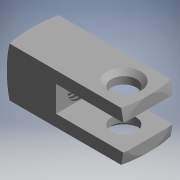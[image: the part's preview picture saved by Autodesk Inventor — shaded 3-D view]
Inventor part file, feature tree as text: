
AUTODESK INVENTOR PART (.ipt)
format: ipt  version: 2017.3 (Build 213256000, 256)  size: 193,024 bytes
history: native  units: mm (DEFAULTED — no unit token found)
features: other x126, sketch x7, revolve x4, extrude x2, thread x1, hole x1
ambient origin geometry x8: Origin, YZ Plane, XZ Plane, XY Plane, X Axis, Y Axis, Z Axis, Center Point
bodies: Solid1 (feature_tree)
feature tree (141):
  extrude  "Extrusion1"  Depth=12.7mm TaperAngle=0.0deg
  extrude  "Extrusion2"  Depth=10.6032mm TaperAngle=0.0deg
  revolve  "Revolution1"  Angle=360.0deg
  thread  "Thread1"  [1 undecoded]
  hole  "Hole1"  [1 undecoded]
  revolve  "Revolution2"  [1 undecoded]
  revolve  "Revolution3"  [1 undecoded]
  revolve  "Revolution4"  [1 undecoded]
  other  "dummy_XY"
  other  "dummy_YZ"
  other  "dummy_ZX"
  other  "dummy_X"
  other  "dummy_Y"
  other  "dummy_Z"
  other  "dummy_Center"
  other  "h1_XY"
  other  "h1_YZ"
  other  "h1_ZX"
  other  "h1_X"
  other  "h1_Y"
  other  "h1_Z"
  other  "h1_Center"
  other  "h2_XY"
  other  "h2_YZ"
  other  "h2_ZX"
  other  "h2_X"
  other  "h2_Y"
  other  "h2_Z"
  other  "h2_Center"
  other  "l1_XY"
  other  "l1_YZ"
  other  "l1_ZX"
  other  "l1_X"
  other  "l1_Y"
  other  "l1_Z"
  other  "l1_Center"
  other  "l11_XY"
  other  "l11_YZ"
  other  "l11_ZX"
  other  "l11_X"
  other  "l11_Y"
  other  "l11_Z"
  other  "l11_Center"
  other  "l12_XY"
  other  "l12_YZ"
  other  "l12_ZX"
  other  "l12_X"
  other  "l12_Y"
  other  "l12_Z"
  other  "l12_Center"
  other  "l2_XY"
  other  "l2_YZ"
  other  "l2_ZX"
  other  "l2_X"
  other  "l2_Y"
  other  "l2_Z"
  other  "l2_Center"
  other  "l21_XY"
  other  "l21_YZ"
  other  "l21_ZX"
  other  "l21_X"
  other  "l21_Y"
  other  "l21_Z"
  other  "l21_Center"
  other  "l22_XY"
  other  "l22_YZ"
  other  "l22_ZX"
  other  "l22_X"
  other  "l22_Y"
  other  "l22_Z"
  other  "l22_Center"
  other  "piston_rod_clevis_XY"
  other  "piston_rod_clevis_YZ"
  other  "piston_rod_clevis_ZX"
  other  "piston_rod_clevis_X"
  other  "piston_rod_clevis_Y"
  other  "piston_rod_clevis_Z"
  other  "piston_rod_clevis_Center"
  other  "rod_clevis_body_XY"
  other  "rod_clevis_body_YZ"
  other  "rod_clevis_body_ZX"
  other  "rod_clevis_body_X"
  other  "rod_clevis_body_Y"
  other  "rod_clevis_body_Z"
  other  "rod_clevis_body_Center"
  other  "th1_XY"
  other  "th1_YZ"
  other  "th1_ZX"
  other  "th1_X"
  other  "th1_Y"
  other  "th1_Z"
  other  "th1_Center"
  other  "th2_XY"
  other  "th2_YZ"
  other  "th2_ZX"
  other  "th2_X"
  other  "th2_Y"
  other  "th2_Z"
  other  "th2_Center"
  other  "to_cylinder_XY"
  other  "to_cylinder_YZ"
  other  "to_cylinder_ZX"
  other  "to_cylinder_X"
  other  "to_cylinder_Y"
  other  "to_cylinder_Z"
  other  "to_cylinder_Center"
  other  "w1_XY"
  other  "w1_YZ"
  other  "w1_ZX"
  other  "w1_X"
  other  "w1_Y"
  other  "w1_Z"
  other  "w1_Center"
  other  "w11_XY"
  other  "w11_YZ"
  other  "w11_ZX"
  other  "w11_X"
  other  "w11_Y"
  other  "w11_Z"
  other  "w11_Center"
  other  "w12_XY"
  other  "w12_YZ"
  other  "w12_ZX"
  other  "w12_X"
  other  "w12_Y"
  other  "w12_Z"
  other  "w12_Center"
  other  "w2_XY"
  other  "w2_YZ"
  other  "w2_ZX"
  other  "w2_X"
  other  "w2_Y"
  other  "w2_Z"
  other  "w2_Center"
  sketch  "Sketch_1"  dims[d0=12.7mm d1=0.0mm d2=12.7mm d3=0.0mm]
  sketch  "Sketch_2"  dims[d4=360.0deg d5=10.6032mm d6=0.0mm]
  sketch  "Sketch_3"  dims[d7=6.79196mm d8=6.0mm d9=4.0mm d10=2.0mm d11=90.0deg d12=1.524mm d13=0.0mm d14=360.0deg d15=360.0deg]
  sketch  "Sketch5"  dims[d16=360.0deg d17=0.0mm d18=0.0mm]
  sketch  "Sketch_5"
  sketch  "Sketch_9"
  sketch  "Sketch_10"
note: 5 required parameter values undecoded (feature->parameter linkage not recoverable at this tier; creation-order binding heuristic only, values carry confidence <= 0.55)
